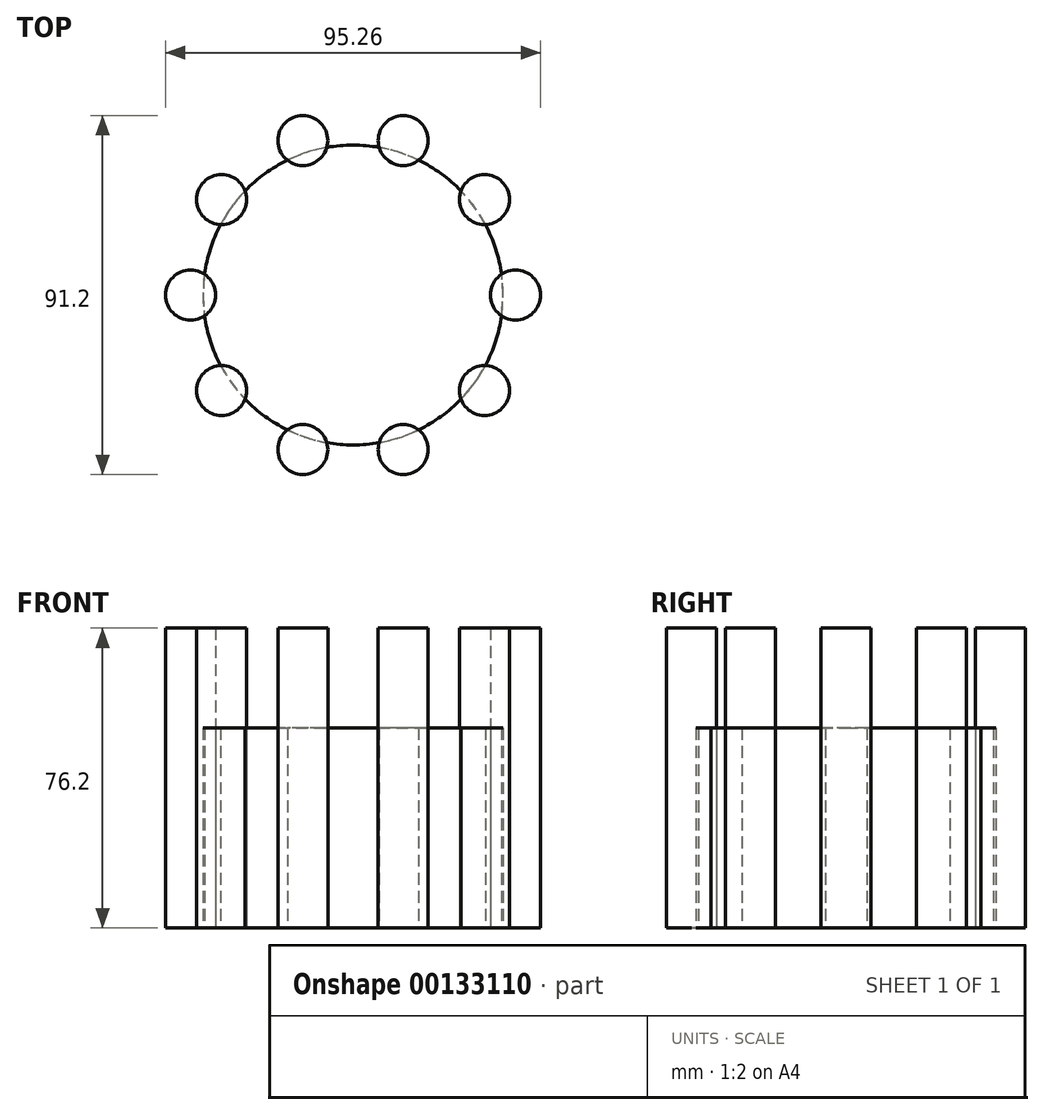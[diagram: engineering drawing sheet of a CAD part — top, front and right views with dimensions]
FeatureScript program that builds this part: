
annotation { "Feature Type Name" : "Feature", "Feature Type Description" : "" }
export const myFeature = defineFeature(function(context is Context, id is Id, definition is map)
    precondition{}
    {
        {
            var Q0;
            Q0=qCreatedBy(makeId("Top.planeOp"),FACE);
            var sketch = newSketch(context, id + "F0", { "sketchPlane" : qUnion([Q0])});
            skCircle(sketch, "E0", {"center": v(0, 0) * mm, "radius": 38.1 * mm});
            skCircle(sketch, "E1", {"center": v(41.28, 0) * mm, "radius": 6.35 * mm});
            skCircle(sketch, "E2.1.0", {"center": v(33.4, -24.26) * mm, "radius": 6.35 * mm});
            skCircle(sketch, "E2.2.0", {"center": v(12.75, -39.25) * mm, "radius": 6.35 * mm});
            skCircle(sketch, "E2.3.0", {"center": v(-12.75, -39.25) * mm, "radius": 6.35 * mm});
            skCircle(sketch, "E2.4.0", {"center": v(-33.4, -24.26) * mm, "radius": 6.35 * mm});
            skCircle(sketch, "E2.5.0", {"center": v(-41.28, 0) * mm, "radius": 6.35 * mm});
            skCircle(sketch, "E2.6.0", {"center": v(-33.4, 24.26) * mm, "radius": 6.35 * mm});
            skCircle(sketch, "E2.7.0", {"center": v(-12.75, 39.25) * mm, "radius": 6.35 * mm});
            skCircle(sketch, "E2.8.0", {"center": v(12.75, 39.25) * mm, "radius": 6.35 * mm});
            skCircle(sketch, "E2.9.0", {"center": v(33.4, 24.26) * mm, "radius": 6.35 * mm});
            skLineSegment(sketch, "E2.anchor1", {"start": v(0, 0) * mm, "end": v(41.28, 0) * mm, "construction": true});
            skLineSegment(sketch, "E2.anchor2", {"start": v(0, 0) * mm, "end": v(33.4, 24.26) * mm, "construction": true});
            skSolve(sketch);
        }
        {
            var Q0;
            {var subQ0=sQuery(id+"F0.wireOp",EDGE,"E2.6.0");var subQ1=sQuery(id+"F0.wireOp",EDGE,"E0");var subQ2=makeQuery(id+"F0.imprint","INTERSECT",VERTEX,{"disambiguationData":[OD(0.0)],"derivedFrom":[subQ1,subQ0]});Q0=makeQuery(id+"F0.imprint","IMPRINT",FACE,{"disambiguationData":[TD([[makeQuery(id+"F0.imprint","IMPRINT",EDGE,{"disambiguationData":[TD([[subQ2,-1.0]])],"derivedFrom":subQ1}),1.0]])]});}
            var Q1;
            {var subQ0=sQuery(id+"F0.wireOp",EDGE,"E2.7.0");var subQ1=sQuery(id+"F0.wireOp",EDGE,"E0");var subQ2=makeQuery(id+"F0.imprint","INTERSECT",VERTEX,{"disambiguationData":[OD(0.0)],"derivedFrom":[subQ1,subQ0]});Q1=makeQuery(id+"F0.imprint","IMPRINT",FACE,{"disambiguationData":[TD([[makeQuery(id+"F0.imprint","IMPRINT",EDGE,{"disambiguationData":[TD([[subQ2,-1.0]])],"derivedFrom":subQ1}),1.0]])]});}
            var Q2;
            {var subQ0=sQuery(id+"F0.wireOp",EDGE,"E2.8.0");var subQ1=sQuery(id+"F0.wireOp",EDGE,"E0");var subQ2=makeQuery(id+"F0.imprint","INTERSECT",VERTEX,{"disambiguationData":[OD(0.0)],"derivedFrom":[subQ1,subQ0]});Q2=makeQuery(id+"F0.imprint","IMPRINT",FACE,{"disambiguationData":[TD([[makeQuery(id+"F0.imprint","IMPRINT",EDGE,{"disambiguationData":[TD([[subQ2,-1.0]])],"derivedFrom":subQ1}),1.0]])]});}
            var Q3;
            {var subQ0=sQuery(id+"F0.wireOp",EDGE,"E2.9.0");var subQ1=sQuery(id+"F0.wireOp",EDGE,"E0");var subQ2=makeQuery(id+"F0.imprint","INTERSECT",VERTEX,{"disambiguationData":[OD(0.0)],"derivedFrom":[subQ1,subQ0]});Q3=makeQuery(id+"F0.imprint","IMPRINT",FACE,{"disambiguationData":[TD([[makeQuery(id+"F0.imprint","IMPRINT",EDGE,{"disambiguationData":[TD([[subQ2,-1.0]])],"derivedFrom":subQ1}),1.0]])]});}
            var Q4;
            {var subQ0=sQuery(id+"F0.wireOp",EDGE,"E1");var subQ1=sQuery(id+"F0.wireOp",EDGE,"E0");var subQ2=makeQuery(id+"F0.imprint","INTERSECT",VERTEX,{"disambiguationData":[OD(0.0)],"derivedFrom":[subQ1,subQ0]});Q4=makeQuery(id+"F0.imprint","IMPRINT",FACE,{"disambiguationData":[TD([[makeQuery(id+"F0.imprint","IMPRINT",EDGE,{"disambiguationData":[TD([[subQ2,1.0]])],"derivedFrom":subQ1}),1.0]])]});}
            var Q5;
            {var subQ0=sQuery(id+"F0.wireOp",EDGE,"E2.1.0");var subQ1=sQuery(id+"F0.wireOp",EDGE,"E0");var subQ2=makeQuery(id+"F0.imprint","INTERSECT",VERTEX,{"disambiguationData":[OD(0.0)],"derivedFrom":[subQ1,subQ0]});Q5=makeQuery(id+"F0.imprint","IMPRINT",FACE,{"disambiguationData":[TD([[makeQuery(id+"F0.imprint","IMPRINT",EDGE,{"disambiguationData":[TD([[subQ2,-1.0]])],"derivedFrom":subQ1}),1.0]])]});}
            var Q6;
            {var subQ0=sQuery(id+"F0.wireOp",EDGE,"E2.2.0");var subQ1=sQuery(id+"F0.wireOp",EDGE,"E0");var subQ2=makeQuery(id+"F0.imprint","INTERSECT",VERTEX,{"disambiguationData":[OD(0.0)],"derivedFrom":[subQ1,subQ0]});Q6=makeQuery(id+"F0.imprint","IMPRINT",FACE,{"disambiguationData":[TD([[makeQuery(id+"F0.imprint","IMPRINT",EDGE,{"disambiguationData":[TD([[subQ2,-1.0]])],"derivedFrom":subQ1}),1.0]])]});}
            var Q7;
            {var subQ0=sQuery(id+"F0.wireOp",EDGE,"E2.4.0");var subQ1=sQuery(id+"F0.wireOp",EDGE,"E0");var subQ2=makeQuery(id+"F0.imprint","INTERSECT",VERTEX,{"disambiguationData":[OD(0.0)],"derivedFrom":[subQ1,subQ0]});Q7=makeQuery(id+"F0.imprint","IMPRINT",FACE,{"disambiguationData":[TD([[makeQuery(id+"F0.imprint","IMPRINT",EDGE,{"disambiguationData":[TD([[subQ2,-1.0]])],"derivedFrom":subQ1}),1.0]])]});}
            var Q8;
            {var subQ0=sQuery(id+"F0.wireOp",EDGE,"E2.5.0");var subQ1=sQuery(id+"F0.wireOp",EDGE,"E0");var subQ2=makeQuery(id+"F0.imprint","INTERSECT",VERTEX,{"disambiguationData":[OD(0.0)],"derivedFrom":[subQ1,subQ0]});Q8=makeQuery(id+"F0.imprint","IMPRINT",FACE,{"disambiguationData":[TD([[makeQuery(id+"F0.imprint","IMPRINT",EDGE,{"disambiguationData":[TD([[subQ2,-1.0]])],"derivedFrom":subQ1}),1.0]])]});}
            var Q9;
            {var subQ1=sQuery(id+"F0.wireOp",EDGE,"E0");var subQ23=sQuery(id+"F0.wireOp",EDGE,"E2.9.0");var subQ24=makeQuery(id+"F0.imprint","INTERSECT",VERTEX,{"disambiguationData":[OD(0.0)],"derivedFrom":[subQ1,subQ23]});Q9=makeQuery(id+"F0.imprint","IMPRINT",FACE,{"disambiguationData":[TD([[makeQuery(id+"F0.imprint","IMPRINT",EDGE,{"disambiguationData":[TD([[subQ24,1.0]])],"derivedFrom":subQ1}),1.0]])]});}
            var Q10;
            {var subQ0=sQuery(id+"F0.wireOp",EDGE,"E2.3.0");var subQ1=sQuery(id+"F0.wireOp",EDGE,"E0");var subQ2=makeQuery(id+"F0.imprint","INTERSECT",VERTEX,{"disambiguationData":[OD(0.0)],"derivedFrom":[subQ1,subQ0]});Q10=makeQuery(id+"F0.imprint","IMPRINT",FACE,{"disambiguationData":[TD([[makeQuery(id+"F0.imprint","IMPRINT",EDGE,{"disambiguationData":[TD([[subQ2,-1.0]])],"derivedFrom":subQ1}),1.0]])]});}
            extrude(context, id + "F1", {"entities" : qUnion([Q0, Q1, Q2, Q3, Q4, Q5, Q6, Q7, Q8, Q9, Q10]), "depth" : 50.8 * mm});
        }
        {
            var Q0;
            {var subQ0=sQuery(id+"F0.wireOp",EDGE,"E2.2.0");var subQ1=sQuery(id+"F0.wireOp",EDGE,"E0");var subQ2=makeQuery(id+"F0.imprint","INTERSECT",VERTEX,{"disambiguationData":[OD(0.0)],"derivedFrom":[subQ1,subQ0]});Q0=makeQuery(id+"F0.imprint","IMPRINT",FACE,{"disambiguationData":[TD([[makeQuery(id+"F0.imprint","IMPRINT",EDGE,{"disambiguationData":[TD([[subQ2,-1.0]])],"derivedFrom":subQ1}),1.0]])]});}
            var Q1;
            {var subQ0=sQuery(id+"F0.wireOp",EDGE,"E2.2.0");var subQ1=sQuery(id+"F0.wireOp",EDGE,"E0");var subQ2=makeQuery(id+"F0.imprint","INTERSECT",VERTEX,{"disambiguationData":[OD(0.0)],"derivedFrom":[subQ1,subQ0]});Q1=makeQuery(id+"F0.imprint","IMPRINT",FACE,{"disambiguationData":[TD([[makeQuery(id+"F0.imprint","IMPRINT",EDGE,{"disambiguationData":[TD([[subQ2,-1.0]])],"derivedFrom":subQ1}),-1.0]])]});}
            var Q2;
            {var subQ0=sQuery(id+"F0.wireOp",EDGE,"E2.1.0");var subQ1=sQuery(id+"F0.wireOp",EDGE,"E0");var subQ2=makeQuery(id+"F0.imprint","INTERSECT",VERTEX,{"disambiguationData":[OD(0.0)],"derivedFrom":[subQ1,subQ0]});Q2=makeQuery(id+"F0.imprint","IMPRINT",FACE,{"disambiguationData":[TD([[makeQuery(id+"F0.imprint","IMPRINT",EDGE,{"disambiguationData":[TD([[subQ2,-1.0]])],"derivedFrom":subQ1}),1.0]])]});}
            var Q3;
            {var subQ0=sQuery(id+"F0.wireOp",EDGE,"E2.1.0");var subQ1=sQuery(id+"F0.wireOp",EDGE,"E0");var subQ2=makeQuery(id+"F0.imprint","INTERSECT",VERTEX,{"disambiguationData":[OD(0.0)],"derivedFrom":[subQ1,subQ0]});Q3=makeQuery(id+"F0.imprint","IMPRINT",FACE,{"disambiguationData":[TD([[makeQuery(id+"F0.imprint","IMPRINT",EDGE,{"disambiguationData":[TD([[subQ2,-1.0]])],"derivedFrom":subQ1}),-1.0]])]});}
            var Q4;
            {var subQ0=sQuery(id+"F0.wireOp",EDGE,"E2.3.0");var subQ1=sQuery(id+"F0.wireOp",EDGE,"E0");var subQ2=makeQuery(id+"F0.imprint","INTERSECT",VERTEX,{"disambiguationData":[OD(0.0)],"derivedFrom":[subQ1,subQ0]});Q4=makeQuery(id+"F0.imprint","IMPRINT",FACE,{"disambiguationData":[TD([[makeQuery(id+"F0.imprint","IMPRINT",EDGE,{"disambiguationData":[TD([[subQ2,-1.0]])],"derivedFrom":subQ1}),1.0]])]});}
            var Q5;
            {var subQ0=sQuery(id+"F0.wireOp",EDGE,"E2.3.0");var subQ1=sQuery(id+"F0.wireOp",EDGE,"E0");var subQ2=makeQuery(id+"F0.imprint","INTERSECT",VERTEX,{"disambiguationData":[OD(0.0)],"derivedFrom":[subQ1,subQ0]});Q5=makeQuery(id+"F0.imprint","IMPRINT",FACE,{"disambiguationData":[TD([[makeQuery(id+"F0.imprint","IMPRINT",EDGE,{"disambiguationData":[TD([[subQ2,-1.0]])],"derivedFrom":subQ1}),-1.0]])]});}
            var Q6;
            {var subQ0=sQuery(id+"F0.wireOp",EDGE,"E2.4.0");var subQ1=sQuery(id+"F0.wireOp",EDGE,"E0");var subQ2=makeQuery(id+"F0.imprint","INTERSECT",VERTEX,{"disambiguationData":[OD(0.0)],"derivedFrom":[subQ1,subQ0]});Q6=makeQuery(id+"F0.imprint","IMPRINT",FACE,{"disambiguationData":[TD([[makeQuery(id+"F0.imprint","IMPRINT",EDGE,{"disambiguationData":[TD([[subQ2,-1.0]])],"derivedFrom":subQ1}),1.0]])]});}
            var Q7;
            {var subQ0=sQuery(id+"F0.wireOp",EDGE,"E2.4.0");var subQ1=sQuery(id+"F0.wireOp",EDGE,"E0");var subQ2=makeQuery(id+"F0.imprint","INTERSECT",VERTEX,{"disambiguationData":[OD(0.0)],"derivedFrom":[subQ1,subQ0]});Q7=makeQuery(id+"F0.imprint","IMPRINT",FACE,{"disambiguationData":[TD([[makeQuery(id+"F0.imprint","IMPRINT",EDGE,{"disambiguationData":[TD([[subQ2,-1.0]])],"derivedFrom":subQ1}),-1.0]])]});}
            var Q8;
            {var subQ0=sQuery(id+"F0.wireOp",EDGE,"E2.5.0");var subQ1=sQuery(id+"F0.wireOp",EDGE,"E0");var subQ2=makeQuery(id+"F0.imprint","INTERSECT",VERTEX,{"disambiguationData":[OD(0.0)],"derivedFrom":[subQ1,subQ0]});Q8=makeQuery(id+"F0.imprint","IMPRINT",FACE,{"disambiguationData":[TD([[makeQuery(id+"F0.imprint","IMPRINT",EDGE,{"disambiguationData":[TD([[subQ2,-1.0]])],"derivedFrom":subQ1}),1.0]])]});}
            var Q9;
            {var subQ0=sQuery(id+"F0.wireOp",EDGE,"E2.5.0");var subQ1=sQuery(id+"F0.wireOp",EDGE,"E0");var subQ2=makeQuery(id+"F0.imprint","INTERSECT",VERTEX,{"disambiguationData":[OD(0.0)],"derivedFrom":[subQ1,subQ0]});Q9=makeQuery(id+"F0.imprint","IMPRINT",FACE,{"disambiguationData":[TD([[makeQuery(id+"F0.imprint","IMPRINT",EDGE,{"disambiguationData":[TD([[subQ2,-1.0]])],"derivedFrom":subQ1}),-1.0]])]});}
            var Q10;
            {var subQ0=sQuery(id+"F0.wireOp",EDGE,"E2.6.0");var subQ1=sQuery(id+"F0.wireOp",EDGE,"E0");var subQ2=makeQuery(id+"F0.imprint","INTERSECT",VERTEX,{"disambiguationData":[OD(0.0)],"derivedFrom":[subQ1,subQ0]});Q10=makeQuery(id+"F0.imprint","IMPRINT",FACE,{"disambiguationData":[TD([[makeQuery(id+"F0.imprint","IMPRINT",EDGE,{"disambiguationData":[TD([[subQ2,-1.0]])],"derivedFrom":subQ1}),1.0]])]});}
            var Q11;
            {var subQ0=sQuery(id+"F0.wireOp",EDGE,"E2.6.0");var subQ1=sQuery(id+"F0.wireOp",EDGE,"E0");var subQ2=makeQuery(id+"F0.imprint","INTERSECT",VERTEX,{"disambiguationData":[OD(0.0)],"derivedFrom":[subQ1,subQ0]});Q11=makeQuery(id+"F0.imprint","IMPRINT",FACE,{"disambiguationData":[TD([[makeQuery(id+"F0.imprint","IMPRINT",EDGE,{"disambiguationData":[TD([[subQ2,-1.0]])],"derivedFrom":subQ1}),-1.0]])]});}
            var Q12;
            {var subQ0=sQuery(id+"F0.wireOp",EDGE,"E2.7.0");var subQ1=sQuery(id+"F0.wireOp",EDGE,"E0");var subQ2=makeQuery(id+"F0.imprint","INTERSECT",VERTEX,{"disambiguationData":[OD(0.0)],"derivedFrom":[subQ1,subQ0]});Q12=makeQuery(id+"F0.imprint","IMPRINT",FACE,{"disambiguationData":[TD([[makeQuery(id+"F0.imprint","IMPRINT",EDGE,{"disambiguationData":[TD([[subQ2,-1.0]])],"derivedFrom":subQ1}),1.0]])]});}
            var Q13;
            {var subQ0=sQuery(id+"F0.wireOp",EDGE,"E2.7.0");var subQ1=sQuery(id+"F0.wireOp",EDGE,"E0");var subQ2=makeQuery(id+"F0.imprint","INTERSECT",VERTEX,{"disambiguationData":[OD(0.0)],"derivedFrom":[subQ1,subQ0]});Q13=makeQuery(id+"F0.imprint","IMPRINT",FACE,{"disambiguationData":[TD([[makeQuery(id+"F0.imprint","IMPRINT",EDGE,{"disambiguationData":[TD([[subQ2,-1.0]])],"derivedFrom":subQ1}),-1.0]])]});}
            var Q14;
            {var subQ0=sQuery(id+"F0.wireOp",EDGE,"E2.8.0");var subQ1=sQuery(id+"F0.wireOp",EDGE,"E0");var subQ2=makeQuery(id+"F0.imprint","INTERSECT",VERTEX,{"disambiguationData":[OD(0.0)],"derivedFrom":[subQ1,subQ0]});Q14=makeQuery(id+"F0.imprint","IMPRINT",FACE,{"disambiguationData":[TD([[makeQuery(id+"F0.imprint","IMPRINT",EDGE,{"disambiguationData":[TD([[subQ2,-1.0]])],"derivedFrom":subQ1}),1.0]])]});}
            var Q15;
            {var subQ0=sQuery(id+"F0.wireOp",EDGE,"E2.8.0");var subQ1=sQuery(id+"F0.wireOp",EDGE,"E0");var subQ2=makeQuery(id+"F0.imprint","INTERSECT",VERTEX,{"disambiguationData":[OD(0.0)],"derivedFrom":[subQ1,subQ0]});Q15=makeQuery(id+"F0.imprint","IMPRINT",FACE,{"disambiguationData":[TD([[makeQuery(id+"F0.imprint","IMPRINT",EDGE,{"disambiguationData":[TD([[subQ2,-1.0]])],"derivedFrom":subQ1}),-1.0]])]});}
            var Q16;
            {var subQ0=sQuery(id+"F0.wireOp",EDGE,"E2.9.0");var subQ1=sQuery(id+"F0.wireOp",EDGE,"E0");var subQ2=makeQuery(id+"F0.imprint","INTERSECT",VERTEX,{"disambiguationData":[OD(0.0)],"derivedFrom":[subQ1,subQ0]});Q16=makeQuery(id+"F0.imprint","IMPRINT",FACE,{"disambiguationData":[TD([[makeQuery(id+"F0.imprint","IMPRINT",EDGE,{"disambiguationData":[TD([[subQ2,-1.0]])],"derivedFrom":subQ1}),-1.0]])]});}
            var Q17;
            {var subQ0=sQuery(id+"F0.wireOp",EDGE,"E2.9.0");var subQ1=sQuery(id+"F0.wireOp",EDGE,"E0");var subQ2=makeQuery(id+"F0.imprint","INTERSECT",VERTEX,{"disambiguationData":[OD(0.0)],"derivedFrom":[subQ1,subQ0]});Q17=makeQuery(id+"F0.imprint","IMPRINT",FACE,{"disambiguationData":[TD([[makeQuery(id+"F0.imprint","IMPRINT",EDGE,{"disambiguationData":[TD([[subQ2,-1.0]])],"derivedFrom":subQ1}),1.0]])]});}
            var Q18;
            {var subQ0=sQuery(id+"F0.wireOp",EDGE,"E1");var subQ1=sQuery(id+"F0.wireOp",EDGE,"E0");var subQ2=makeQuery(id+"F0.imprint","INTERSECT",VERTEX,{"disambiguationData":[OD(0.0)],"derivedFrom":[subQ1,subQ0]});Q18=makeQuery(id+"F0.imprint","IMPRINT",FACE,{"disambiguationData":[TD([[makeQuery(id+"F0.imprint","IMPRINT",EDGE,{"disambiguationData":[TD([[subQ2,1.0]])],"derivedFrom":subQ1}),1.0]])]});}
            var Q19;
            {var subQ0=sQuery(id+"F0.wireOp",EDGE,"E1");var subQ1=sQuery(id+"F0.wireOp",EDGE,"E0");var subQ2=makeQuery(id+"F0.imprint","INTERSECT",VERTEX,{"disambiguationData":[OD(0.0)],"derivedFrom":[subQ1,subQ0]});Q19=makeQuery(id+"F0.imprint","IMPRINT",FACE,{"disambiguationData":[TD([[makeQuery(id+"F0.imprint","IMPRINT",EDGE,{"disambiguationData":[TD([[subQ2,1.0]])],"derivedFrom":subQ1}),-1.0]])]});}
            extrude(context, id + "F2", {"entities" : qUnion([Q0, Q1, Q2, Q3, Q4, Q5, Q6, Q7, Q8, Q9, Q10, Q11, Q12, Q13, Q14, Q15, Q16, Q17, Q18, Q19]), "depth" : 76.2 * mm});
        }
        {
            var Q0;
            Q0=makeQuery(id+"F2.opExtrude","SWEPT_BODY",BODY,{"disambiguationData":[OSD([sQuery(id+"F0.wireOp",EDGE,"E2.5.0")])]});
            var Q1;
            Q1=makeQuery(id+"F1.opExtrude","SWEPT_BODY",BODY,{"disambiguationData":[OSD([sQuery(id+"F0.wireOp",EDGE,"E0")])]});
            booleanBodies(context, id + "F3", {"operationType" : BooleanOperationType.INTERSECTION, "tools" : qUnion([Q0, Q1]), "keepTools" : true});
        }
        {
            var Q0;
            Q0=makeQuery(id+"F2.opExtrude","SWEPT_BODY",BODY,{"disambiguationData":[OSD([sQuery(id+"F0.wireOp",EDGE,"E2.6.0")])]});
            var Q1;
            Q1=makeQuery(id+"F1.opExtrude","SWEPT_BODY",BODY,{"disambiguationData":[OSD([sQuery(id+"F0.wireOp",EDGE,"E0")])]});
            booleanBodies(context, id + "F4", {"operationType" : BooleanOperationType.INTERSECTION, "tools" : qUnion([Q0, Q1]), "keepTools" : true});
        }
        {
            var Q0;
            Q0=makeQuery(id+"F2.opExtrude","SWEPT_BODY",BODY,{"disambiguationData":[OSD([sQuery(id+"F0.wireOp",EDGE,"E2.7.0")])]});
            var Q1;
            Q1=makeQuery(id+"F1.opExtrude","SWEPT_BODY",BODY,{"disambiguationData":[OSD([sQuery(id+"F0.wireOp",EDGE,"E0")])]});
            booleanBodies(context, id + "F5", {"operationType" : BooleanOperationType.INTERSECTION, "tools" : qUnion([Q0, Q1]), "keepTools" : true});
        }
        {
            var Q0;
            Q0=makeQuery(id+"F2.opExtrude","SWEPT_BODY",BODY,{"disambiguationData":[OSD([sQuery(id+"F0.wireOp",EDGE,"E2.8.0")])]});
            var Q1;
            Q1=makeQuery(id+"F1.opExtrude","SWEPT_BODY",BODY,{"disambiguationData":[OSD([sQuery(id+"F0.wireOp",EDGE,"E0")])]});
            booleanBodies(context, id + "F6", {"operationType" : BooleanOperationType.INTERSECTION, "tools" : qUnion([Q0, Q1]), "keepTools" : true});
        }
        {
            var Q0;
            Q0=makeQuery(id+"F2.opExtrude","SWEPT_BODY",BODY,{"disambiguationData":[OSD([sQuery(id+"F0.wireOp",EDGE,"E2.9.0")])]});
            var Q1;
            Q1=makeQuery(id+"F1.opExtrude","SWEPT_BODY",BODY,{"disambiguationData":[OSD([sQuery(id+"F0.wireOp",EDGE,"E0")])]});
            booleanBodies(context, id + "F7", {"operationType" : BooleanOperationType.INTERSECTION, "tools" : qUnion([Q0, Q1]), "keepTools" : true});
        }
        {
            var Q0;
            Q0=makeQuery(id+"F2.opExtrude","SWEPT_BODY",BODY,{"disambiguationData":[OSD([sQuery(id+"F0.wireOp",EDGE,"E1")])]});
            var Q1;
            Q1=makeQuery(id+"F1.opExtrude","SWEPT_BODY",BODY,{"disambiguationData":[OSD([sQuery(id+"F0.wireOp",EDGE,"E0")])]});
            booleanBodies(context, id + "F8", {"operationType" : BooleanOperationType.INTERSECTION, "tools" : qUnion([Q0, Q1]), "keepTools" : true});
        }
        {
            var Q0;
            Q0=makeQuery(id+"F2.opExtrude","SWEPT_BODY",BODY,{"disambiguationData":[OSD([sQuery(id+"F0.wireOp",EDGE,"E2.1.0")])]});
            var Q1;
            Q1=makeQuery(id+"F1.opExtrude","SWEPT_BODY",BODY,{"disambiguationData":[OSD([sQuery(id+"F0.wireOp",EDGE,"E0")])]});
            booleanBodies(context, id + "F9", {"operationType" : BooleanOperationType.INTERSECTION, "tools" : qUnion([Q0, Q1]), "keepTools" : true});
        }
        {
            var Q0;
            Q0=makeQuery(id+"F2.opExtrude","SWEPT_BODY",BODY,{"disambiguationData":[OSD([sQuery(id+"F0.wireOp",EDGE,"E2.2.0")])]});
            var Q1;
            Q1=makeQuery(id+"F1.opExtrude","SWEPT_BODY",BODY,{"disambiguationData":[OSD([sQuery(id+"F0.wireOp",EDGE,"E0")])]});
            booleanBodies(context, id + "F10", {"operationType" : BooleanOperationType.INTERSECTION, "tools" : qUnion([Q0, Q1]), "keepTools" : true});
        }
        {
            var Q0;
            Q0=makeQuery(id+"F2.opExtrude","SWEPT_BODY",BODY,{"disambiguationData":[OSD([sQuery(id+"F0.wireOp",EDGE,"E2.3.0")])]});
            var Q1;
            Q1=makeQuery(id+"F1.opExtrude","SWEPT_BODY",BODY,{"disambiguationData":[OSD([sQuery(id+"F0.wireOp",EDGE,"E0")])]});
            booleanBodies(context, id + "F11", {"operationType" : BooleanOperationType.INTERSECTION, "tools" : qUnion([Q0, Q1]), "keepTools" : true});
        }
        {
            var Q0;
            Q0=makeQuery(id+"F2.opExtrude","SWEPT_BODY",BODY,{"disambiguationData":[OSD([sQuery(id+"F0.wireOp",EDGE,"E2.4.0")])]});
            var Q1;
            Q1=makeQuery(id+"F1.opExtrude","SWEPT_BODY",BODY,{"disambiguationData":[OSD([sQuery(id+"F0.wireOp",EDGE,"E0")])]});
            booleanBodies(context, id + "F12", {"operationType" : BooleanOperationType.INTERSECTION, "tools" : qUnion([Q0, Q1]), "keepTools" : true});
        }
    });
